# Revit family: Haworth_JiveTable_CrescentSwivelBase
name_source: partatom
category: Furniture Systems
revit_build: Autodesk Revit 2018 (Build: 20170223_1515(x64)
units: mm (PartAtom-declared; Revit-internal decimal feet)

## family parameters
Always vertical = Yes
Cut with Voids When Loaded = No
OmniClass Number = 23.40.70.14.64.21
OmniClass Title = Systems Furniture
Part Type = Normal
Room Calculation Point = No
Round Connector Dimension = Use Diameter
Shared = No
Work Plane-Based = No

## types (6) — shared parameters
Actual Height = 29"
Assembly Code = E2020200
Leg Finish = Haworth _ Paint _ Graphite
Leg Height = 27 13/16"
Manufacturer = Haworth, Inc.
Max. Depth = 36"
Max. Height = 29"
Max. Width = 59"
Min. Depth = 24"
Min. Height = 29"
Min. Width = 42"
Model = Haworth Jive
Revision Number = 0
Size = Verify Final Dim. w/ Haworth
Standard Depths = 24, 30, 36 in.
Standard Widths = 60, 72, 84 in.
Table Edge Finish = Haworth _ Laminate _ Putty H-AA
Table Finish = Haworth _ Laminate _ Putty H-AA
Table Thickness = 1 3/16"
URL = http://www.haworth.com
URL - Product = https://www.haworth.com
Warranty = http://haworth.com

## per-type parameters (varying)
| type | 24x60 | 30x72 | 36x84 | Actual Depth | Actual Width | Casters | Description | Glides |
| 24d 60w - With Casters | Yes | No | No | 24" | 42" | Yes | Haworth Jive Table - Swivel Base - Crescent - 24d 60w - With Casters | No |
| 30d 72w - With Casters | No | Yes | No | 30" | 50" | Yes | Haworth Jive Table - Swivel Base - Crescent - 30d 72w - With Casters | No |
| 36d 84w - With Casters | No | No | Yes | 36" | 59" | Yes | Haworth Jive Table - Swivel Base - Crescent - 36d 84w - With Casters | No |
| 24d 60w - With Glides | Yes | No | No | 24" | 42" | No | Haworth Jive Table - Swivel Base - Crescent - 24d 60w - With Glides | Yes |
| 30d 72w - With Glides | No | Yes | No | 30" | 50" | No | Haworth Jive Table - Swivel Base - Crescent - 30d 72w - With Glides | Yes |
| 36d 84w - With Glides | No | No | Yes | 36" | 59" | No | Haworth Jive Table - Swivel Base - Crescent - 36d 84w - With Glides | Yes |

## geometry (parser evidence)
native form markers: Sweep x5
no freeform markers — native parametric forms only
